# Revit family: PGL
name_source: partatom
category: Lighting Fixtures
units: mm (PartAtom-declared; Revit-internal decimal feet)

## family parameters
Cut with Voids When Loaded = No
Host = Face
Light Source = Yes
OmniClass Number = 23.80.70.11
OmniClass Title = Luminaries for Internal Lighting
Part Type = Normal
Room Calculation Point = No
Round Connector Dimension = Use Diameter
Shared = No

## types (2) — shared parameters
Apparent Load = 0 VA
Assembly Code = D5020200
Certifications = UL & CSA
Color Filter = 16777215
Default Elevation = 48"
Description = Perimaliter PGL
Dimming Lamp Color Temperature Shift = <None>
Emit Shape Visible in Rendering = No
Emit from Rectangle Length = 6"
Emit from Rectangle Width = 13"
Frequency Rating = 50/60 Hz
Glass Material = White Glass
Housing Material = Powdercoat - Dark Bronze
Lamp = LED
Load Classification = Lighting
Manufacturer = EXO
Model = PGL
Mounting Type = Wall Mount (surface)
Wall (surface)
Wall (surface)
Wall Mount (Surface)
Power Factor = 1
Tilt Angle = 0.00°
URL = https://www.currentlighting.com
Voltage = 120 V
Wattage Comments = 250W & 400W

## per-type parameters (varying)
| type | Photometric Web File |
| PGL-400 | PGL400H-x2x.ies |
| PGL-250 | PGL250H-x2x.ies |

## geometry (parser evidence)
native form markers: Blend x7, Sweep x2
no freeform markers — native parametric forms only
